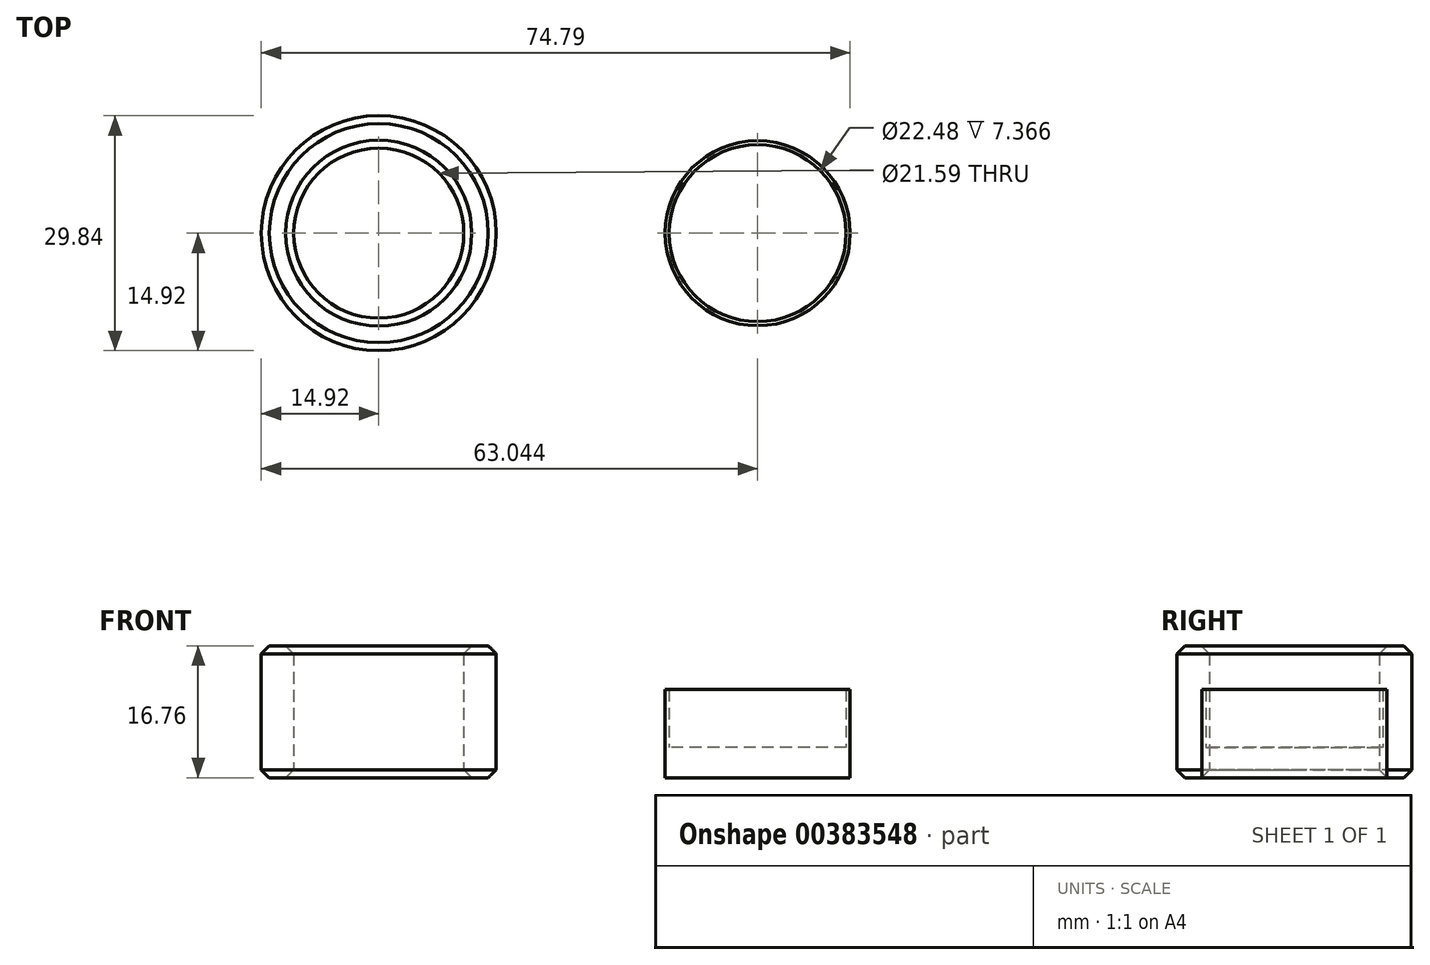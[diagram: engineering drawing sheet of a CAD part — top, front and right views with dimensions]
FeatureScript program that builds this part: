
annotation { "Feature Type Name" : "Feature", "Feature Type Description" : "" }
export const myFeature = defineFeature(function(context is Context, id is Id, definition is map)
    precondition{}
    {
        {
            var Q0;
            Q0=qCreatedBy(makeId("Top.planeOp"),FACE);
            var sketch = newSketch(context, id + "F0", { "sketchPlane" : qUnion([Q0])});
            skCircle(sketch, "E0", {"center": v(0, 0) * mm, "radius": 10.8 * mm});
            skCircle(sketch, "E1", {"center": v(0, 0) * mm, "radius": 14.92 * mm});
            skSolve(sketch);
        }
        {
            var Q0;
            Q0=makeQuery(id+"F0.imprint","IMPRINT",FACE,{"disambiguationData":[TD([[makeQuery(id+"F0.imprint","IMPRINT",EDGE,{"derivedFrom":sQuery(id+"F0.wireOp",EDGE,"E0")}),-1.0]])]});
            extrude(context, id + "F1", {"entities" : qUnion([Q0]), "depth" : 16.76 * mm});
        }
        {
            var Q0;
            Q0=makeQuery(id+"F1.opExtrude","CAP_EDGE",EDGE,{"disambiguationData":[OSD([sQuery(id+"F0.wireOp",EDGE,"E0")])],"isStart":false});
            var Q1;
            Q1=makeQuery(id+"F1.opExtrude","CAP_EDGE",EDGE,{"disambiguationData":[OSD([sQuery(id+"F0.wireOp",EDGE,"E1")])],"isStart":false});
            var Q2;
            Q2=makeQuery(id+"F1.opExtrude","CAP_EDGE",EDGE,{"disambiguationData":[OSD([sQuery(id+"F0.wireOp",EDGE,"E0")])],"isStart":true});
            var Q3;
            Q3=makeQuery(id+"F1.opExtrude","CAP_EDGE",EDGE,{"disambiguationData":[OSD([sQuery(id+"F0.wireOp",EDGE,"E1")])],"isStart":true});
            chamfer(context, id + "F2", {"entities" : qUnion([Q0, Q1, Q2, Q3]), "width" : 1.02 * mm, "tangentPropagation" : true});
        }
        {
            var Q0;
            Q0=qCreatedBy(makeId("Top.planeOp"),FACE);
            var sketch = newSketch(context, id + "F3", { "sketchPlane" : qUnion([Q0])});
            skCircle(sketch, "E2", {"center": v(48.12, 0) * mm, "radius": 11.75 * mm});
            skSolve(sketch);
        }
        {
            var Q0;
            Q0=makeQuery(id+"F3.imprint","IMPRINT",FACE,{"disambiguationData":[TD([[makeQuery(id+"F3.imprint","IMPRINT",EDGE,{"derivedFrom":sQuery(id+"F3.wireOp",EDGE,"E2")}),1.0]])]});
            extrude(context, id + "F4", {"entities" : qUnion([Q0]), "depth" : 3.84 * mm});
        }
        {
            var Q0;
            Q0=makeQuery(id+"F4.opExtrude","CAP_FACE",FACE,{"disambiguationData":[OSD([sQuery(id+"F3.wireOp",EDGE,"E2")])],"isStart":false});
            var sketch = newSketch(context, id + "F5", { "sketchPlane" : qUnion([Q0])});
            skCircle(sketch, "E3", {"center": v(48.12, 0) * mm, "radius": 11.24 * mm});
            skSolve(sketch);
        }
        {
            var Q0;
            Q0=makeQuery(id+"F5.imprint","IMPRINT",FACE,{"disambiguationData":[TD([[makeQuery(id+"F5.imprint","IMPRINT",EDGE,{"derivedFrom":sQuery(id+"F5.wireOp",EDGE,"E3")}),-1.0]])]});
            extrude(context, id + "F6", {"entities" : qUnion([Q0]), "operationType" : NewBodyOperationType.ADD, "depth" : 7.37 * mm});
        }
    });
